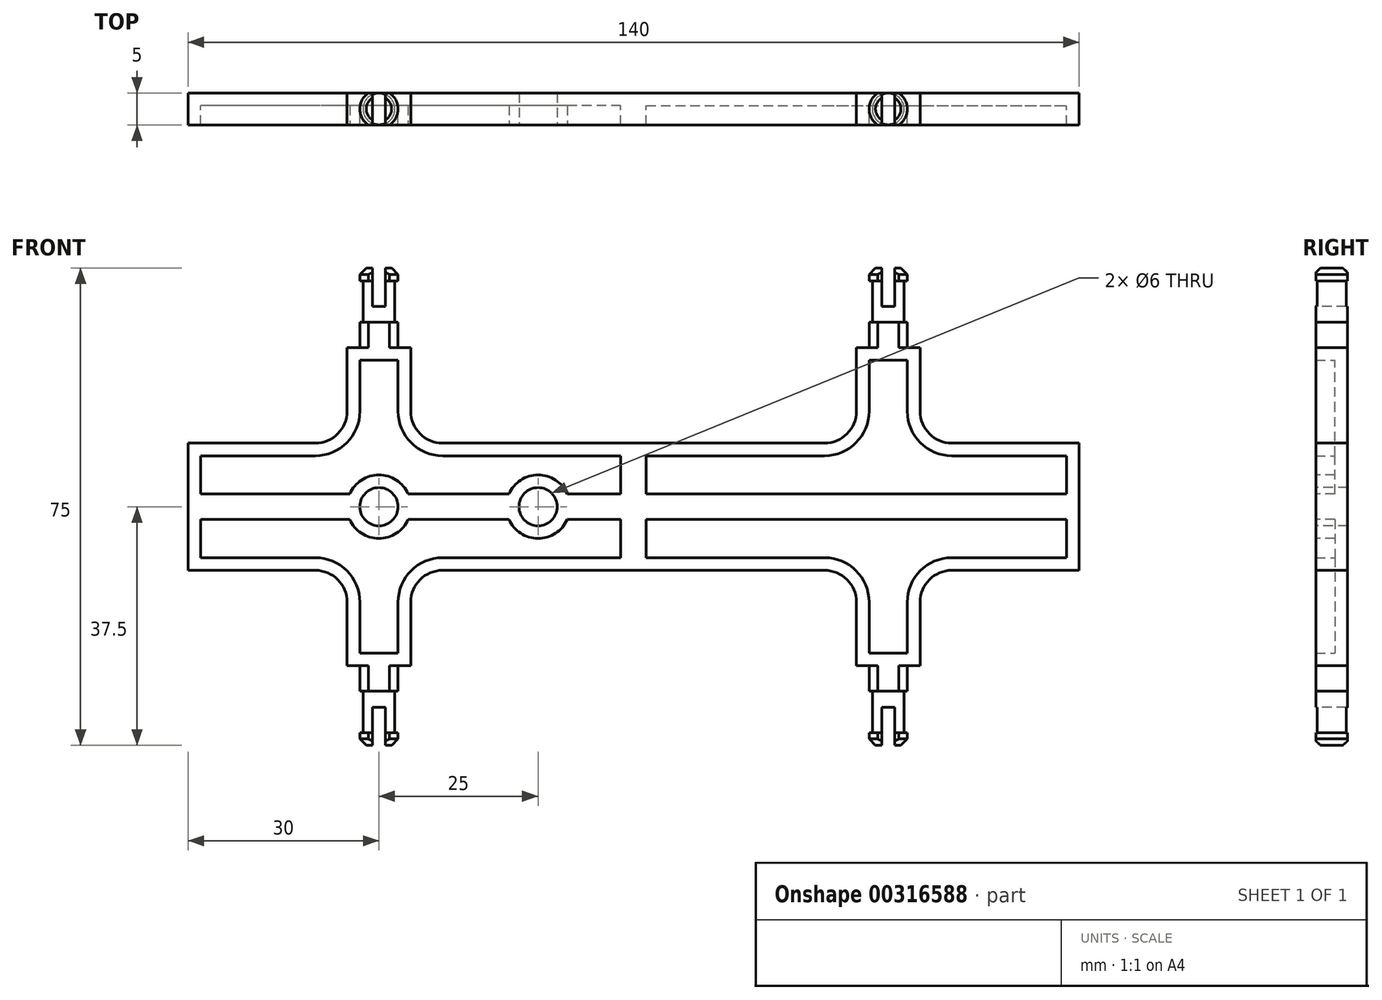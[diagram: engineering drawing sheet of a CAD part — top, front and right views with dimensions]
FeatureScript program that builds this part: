
annotation { "Feature Type Name" : "Feature", "Feature Type Description" : "" }
export const myFeature = defineFeature(function(context is Context, id is Id, definition is map)
    precondition{}
    {
        {
            var Q0;
            Q0=qCreatedBy(makeId("Front.planeOp"),FACE);
            var sketch = newSketch(context, id + "F0", { "sketchPlane" : qUnion([Q0])});
            skLineSegment(sketch, "E0.bottom", {"start": v(0, 0) * mm, "end": v(70, 0) * mm});
            skLineSegment(sketch, "E0.top", {"start": v(0, 10) * mm, "end": v(30, 10) * mm});
            skLineSegment(sketch, "E0.left", {"start": v(0, 0) * mm, "end": v(0, 10) * mm});
            skLineSegment(sketch, "E0.right", {"start": v(70, 0) * mm, "end": v(70, 10) * mm});
            skLineSegment(sketch, "E1.top", {"start": v(35, 25) * mm, "end": v(45, 25) * mm});
            skLineSegment(sketch, "E1.left", {"start": v(35, 15) * mm, "end": v(35, 25) * mm});
            skLineSegment(sketch, "E1.right", {"start": v(45, 15) * mm, "end": v(45, 25) * mm});
            skLineSegment(sketch, "E2.trimOffspring", {"start": v(50, 10) * mm, "end": v(70, 10) * mm});
            skPoint(sketch, "E3.visualSharp", {"position": v(35, 10) * mm});
            skArc(sketch, "E3.filletArc", {"start": v(30, 10) * mm, "mid": v(33.54, 11.46) * mm, "end": v(35, 15) * mm});
            skPoint(sketch, "E4.visualSharp", {"position": v(45, 10) * mm});
            skArc(sketch, "E4.filletArc", {"start": v(45, 15) * mm, "mid": v(46.46, 11.46) * mm, "end": v(50, 10) * mm});
            skSolve(sketch);
        }
        {
            var Q0;
            Q0 = qSketchRegion(id + "F0", true);
            extrude(context, id + "F1", {"entities" : qUnion([Q0]), "endBound" : BoundingType.SYMMETRIC, "depth" : 5 * mm});
        }
        {
            var Q0;
            Q0=makeQuery(id+"F1.opExtrude","CAP_FACE",FACE,{"disambiguationData":[OSD([sQuery(id+"F0.wireOp",EDGE,"E0.bottom"),sQuery(id+"F0.wireOp",EDGE,"E0.top"),sQuery(id+"F0.wireOp",EDGE,"E0.left"),sQuery(id+"F0.wireOp",EDGE,"E0.right"),sQuery(id+"F0.wireOp",EDGE,"E1.top"),sQuery(id+"F0.wireOp",EDGE,"E1.left"),sQuery(id+"F0.wireOp",EDGE,"E1.right"),sQuery(id+"F0.wireOp",EDGE,"E2.trimOffspring"),sQuery(id+"F0.wireOp",EDGE,"E3.filletArc")])],"isStart":false});
            shell(context, id + "F2", {"entities" : qUnion([Q0]), "thickness" : 2 * mm});
        }
        {
            var Q0;
            Q0=qCreatedBy(makeId("Front.planeOp"),FACE);
            var sketch = newSketch(context, id + "F3", { "sketchPlane" : qUnion([Q0])});
            skLineSegment(sketch, "E5", {"start": v(40, 25) * mm, "end": v(40, 37.5) * mm});
            skLineSegment(sketch, "E6", {"start": v(40, 37.5) * mm, "end": v(37, 37.5) * mm});
            skLineSegment(sketch, "E7", {"start": v(37, 37.5) * mm, "end": v(37, 35.5) * mm});
            skLineSegment(sketch, "E8", {"start": v(37, 35.5) * mm, "end": v(37.5, 35.5) * mm});
            skLineSegment(sketch, "E9", {"start": v(37.5, 35.5) * mm, "end": v(37.5, 29) * mm});
            skLineSegment(sketch, "E10", {"start": v(37.5, 29) * mm, "end": v(37, 29) * mm});
            skLineSegment(sketch, "E11", {"start": v(37, 29) * mm, "end": v(37, 25) * mm});
            skLineSegment(sketch, "E12", {"start": v(37, 25) * mm, "end": v(40, 25) * mm});
            skSolve(sketch);
        }
        {
            var Q0;
            Q0 = qSketchRegion(id + "F3", true);
            var Q1;
            Q1=sQuery(id+"F3.wireOp",EDGE,"E5");
            revolve(context, id + "F4", {"operationType" : NewBodyOperationType.ADD, "entities" : qUnion([Q0]), "axis" : qUnion([Q1]), "revolveType" : RevolveType.FULL});
        }
        {
            var Q0;
            Q0=makeQuery(id+"F4.opRevolve","SWEPT_EDGE",EDGE,{"disambiguationData":[OSD([sQuery(id+"F3.wireOp",EDGE,"E6"),sQuery(id+"F3.wireOp",EDGE,"E7")])]});
            chamfer(context, id + "F5", {"entities" : qUnion([Q0]), "width" : 1 * mm, "tangentPropagation" : true});
        }
        {
            var Q0;
            Q0=makeQuery(id+"F4.opRevolve","SWEPT_FACE",FACE,{"disambiguationData":[OSD([sQuery(id+"F3.wireOp",EDGE,"E6")])]});
            var sketch = newSketch(context, id + "F6", { "sketchPlane" : qUnion([Q0])});
            skLineSegment(sketch, "E13.bottom", {"start": v(-1.8, -2.5) * mm, "end": v(71.95, -2.5) * mm});
            skLineSegment(sketch, "E13.top", {"start": v(-1.8, 2.5) * mm, "end": v(71.95, 2.5) * mm});
            skLineSegment(sketch, "E13.left", {"start": v(-1.8, -2.5) * mm, "end": v(-1.8, 2.5) * mm});
            skLineSegment(sketch, "E13.right", {"start": v(71.95, -2.5) * mm, "end": v(71.95, 2.5) * mm});
            skSolve(sketch);
        }
        {
            var Q0;
            Q0 = qSketchRegion(id + "F6", true);
            extrude(context, id + "F7", {"entities" : qUnion([Q0]), "operationType" : NewBodyOperationType.INTERSECT, "endBound" : BoundingType.THROUGH_ALL, "oppositeDirection" : true, "depth" : 25 * mm});
        }
        {
            var Q0;
            Q0=makeQuery(id+"F4.opRevolve","SWEPT_FACE",FACE,{"disambiguationData":[OSD([sQuery(id+"F3.wireOp",EDGE,"E6")])]});
            var sketch = newSketch(context, id + "F8", { "sketchPlane" : qUnion([Q0])});
            skLineSegment(sketch, "E14.bottom", {"start": v(39, 3.52) * mm, "end": v(41, 3.52) * mm});
            skLineSegment(sketch, "E14.top", {"start": v(39, -3.89) * mm, "end": v(41, -3.89) * mm});
            skLineSegment(sketch, "E14.left", {"start": v(39, 3.52) * mm, "end": v(39, -3.89) * mm});
            skLineSegment(sketch, "E14.right", {"start": v(41, 3.52) * mm, "end": v(41, -3.89) * mm});
            skSolve(sketch);
        }
        {
            var Q0;
            Q0 = qSketchRegion(id + "F8", true);
            extrude(context, id + "F9", {"entities" : qUnion([Q0]), "operationType" : NewBodyOperationType.REMOVE, "oppositeDirection" : true, "depth" : 6 * mm});
        }
        {
            var Q0;
            Q0=makeQuery(id+"F1.opExtrude","SWEPT_BODY",BODY,{"disambiguationData":[OSD([sQuery(id+"F0.wireOp",EDGE,"E0.bottom"),sQuery(id+"F0.wireOp",EDGE,"E0.top"),sQuery(id+"F0.wireOp",EDGE,"E0.left"),sQuery(id+"F0.wireOp",EDGE,"E0.right"),sQuery(id+"F0.wireOp",EDGE,"E1.top"),sQuery(id+"F0.wireOp",EDGE,"E1.left"),sQuery(id+"F0.wireOp",EDGE,"E1.right"),sQuery(id+"F0.wireOp",EDGE,"E2.trimOffspring"),sQuery(id+"F0.wireOp",EDGE,"E3.filletArc")])]});
            var Q1;
            Q1=qCreatedBy(makeId("Top.planeOp"),FACE);
            mirror(context, id + "F10", {"operationType" : NewBodyOperationType.ADD, "entities" : qUnion([Q0]), "mirrorPlane" : qUnion([Q1])});
        }
        {
            var Q0;
            Q0=makeQuery(id+"F1.opExtrude","SWEPT_BODY",BODY,{"disambiguationData":[OSD([sQuery(id+"F0.wireOp",EDGE,"E0.bottom"),sQuery(id+"F0.wireOp",EDGE,"E0.top"),sQuery(id+"F0.wireOp",EDGE,"E0.left"),sQuery(id+"F0.wireOp",EDGE,"E0.right"),sQuery(id+"F0.wireOp",EDGE,"E1.top"),sQuery(id+"F0.wireOp",EDGE,"E1.left"),sQuery(id+"F0.wireOp",EDGE,"E1.right"),sQuery(id+"F0.wireOp",EDGE,"E2.trimOffspring"),sQuery(id+"F0.wireOp",EDGE,"E3.filletArc")])]});
            var Q1;
            Q1=qCreatedBy(makeId("Right.planeOp"),FACE);
            mirror(context, id + "F11", {"operationType" : NewBodyOperationType.ADD, "entities" : qUnion([Q0]), "mirrorPlane" : qUnion([Q1])});
        }
        {
            var Q0;
            {var subQ0=makeQuery(id+"F7.boolean.opBoolean","MERGE",FACE,{"derivedFrom":[makeQuery(id+"F1.opExtrude","CAP_FACE",FACE,{"disambiguationData":[OSD([sQuery(id+"F0.wireOp",EDGE,"E0.bottom"),sQuery(id+"F0.wireOp",EDGE,"E0.top"),sQuery(id+"F0.wireOp",EDGE,"E0.left"),sQuery(id+"F0.wireOp",EDGE,"E0.right"),sQuery(id+"F0.wireOp",EDGE,"E1.top"),sQuery(id+"F0.wireOp",EDGE,"E1.left"),sQuery(id+"F0.wireOp",EDGE,"E1.right"),sQuery(id+"F0.wireOp",EDGE,"E2.trimOffspring"),sQuery(id+"F0.wireOp",EDGE,"E3.filletArc")])],"isStart":false}),makeQuery(id+"F7.boolean.toolComplement.opBoolean","COPY",FACE,{"derivedFrom":makeQuery(id+"F7.opExtrude","SWEPT_FACE",FACE,{"disambiguationData":[OSD([sQuery(id+"F6.wireOp",EDGE,"E13.bottom")])]})})]});var subQ1=makeQuery(id+"F10.boolean.opBoolean","MERGE",FACE,{"derivedFrom":[subQ0,makeQuery(id+"F10.opPattern","COPY",FACE,{"derivedFrom":subQ0,"instanceName":"1"})]});Q0=makeQuery(id+"F11.boolean.opBoolean","MERGE",FACE,{"derivedFrom":[subQ1,makeQuery(id+"F11.opPattern","COPY",FACE,{"derivedFrom":subQ1,"instanceName":"1"})]});}
            var sketch = newSketch(context, id + "F12", { "sketchPlane" : qUnion([Q0])});
            skCircle(sketch, "E15", {"center": v(-40, 0) * mm, "radius": 5 * mm});
            skCircle(sketch, "E16", {"center": v(-15, 0) * mm, "radius": 5 * mm});
            skSolve(sketch);
        }
        {
            var Q0;
            Q0 = qSketchRegion(id + "F12", true);
            extrude(context, id + "F13", {"entities" : qUnion([Q0]), "operationType" : NewBodyOperationType.ADD, "endBound" : BoundingType.UP_TO_NEXT, "oppositeDirection" : true, "depth" : 25 * mm});
        }
        {
            var Q0;
            {var subQ0=makeQuery(id+"F7.boolean.opBoolean","MERGE",FACE,{"derivedFrom":[makeQuery(id+"F1.opExtrude","CAP_FACE",FACE,{"disambiguationData":[OSD([sQuery(id+"F0.wireOp",EDGE,"E0.bottom"),sQuery(id+"F0.wireOp",EDGE,"E0.top"),sQuery(id+"F0.wireOp",EDGE,"E0.left"),sQuery(id+"F0.wireOp",EDGE,"E0.right"),sQuery(id+"F0.wireOp",EDGE,"E1.top"),sQuery(id+"F0.wireOp",EDGE,"E1.left"),sQuery(id+"F0.wireOp",EDGE,"E1.right"),sQuery(id+"F0.wireOp",EDGE,"E2.trimOffspring"),sQuery(id+"F0.wireOp",EDGE,"E3.filletArc")])],"isStart":false}),makeQuery(id+"F7.boolean.toolComplement.opBoolean","COPY",FACE,{"derivedFrom":makeQuery(id+"F7.opExtrude","SWEPT_FACE",FACE,{"disambiguationData":[OSD([sQuery(id+"F6.wireOp",EDGE,"E13.bottom")])]})})]});var subQ1=makeQuery(id+"F10.boolean.opBoolean","MERGE",FACE,{"derivedFrom":[subQ0,makeQuery(id+"F10.opPattern","COPY",FACE,{"derivedFrom":subQ0,"instanceName":"1"})]});Q0=makeQuery(id+"F13.boolean.opBoolean","MERGE",FACE,{"derivedFrom":[makeQuery(id+"F11.boolean.opBoolean","MERGE",FACE,{"derivedFrom":[subQ1,makeQuery(id+"F11.opPattern","COPY",FACE,{"derivedFrom":subQ1,"instanceName":"1"})]}),makeQuery(id+"F13.opExtrude","CAP_FACE",FACE,{"disambiguationData":[OSD([sQuery(id+"F12.wireOp",EDGE,"E15")])],"isStart":true}),makeQuery(id+"F13.opExtrude","CAP_FACE",FACE,{"disambiguationData":[OSD([sQuery(id+"F12.wireOp",EDGE,"E16")])],"isStart":true})]});}
            var sketch = newSketch(context, id + "F14", { "sketchPlane" : qUnion([Q0])});
            skPoint(sketch, "E17", {"position": v(-40, 0) * mm});
            skPoint(sketch, "E18", {"position": v(-15, 0) * mm});
            skSolve(sketch);
        }
        {
            var Q0;
            Q0=sQuery(id+"F14.wireOp",VERTEX,"E17");
            var Q1;
            Q1=sQuery(id+"F14.wireOp",VERTEX,"E18");
            var Q2;
            Q2=makeQuery(id+"F1.opExtrude","SWEPT_BODY",BODY,{"disambiguationData":[OSD([sQuery(id+"F0.wireOp",EDGE,"E0.bottom"),sQuery(id+"F0.wireOp",EDGE,"E0.top"),sQuery(id+"F0.wireOp",EDGE,"E0.left"),sQuery(id+"F0.wireOp",EDGE,"E0.right"),sQuery(id+"F0.wireOp",EDGE,"E1.top"),sQuery(id+"F0.wireOp",EDGE,"E1.left"),sQuery(id+"F0.wireOp",EDGE,"E1.right"),sQuery(id+"F0.wireOp",EDGE,"E2.trimOffspring"),sQuery(id+"F0.wireOp",EDGE,"E3.filletArc")])]});
            hole(context, id + "F15", {"style" : HoleStyle.SIMPLE, "endStyle" : HoleEndStyle.THROUGH, "holeDiameter" : 6 * mm, "tappedDepth" : 12 * mm, "tapClearance" : 3, "locations" : qUnion([Q0, Q1]), "scope" : qUnion([Q2])});
        }
    });
